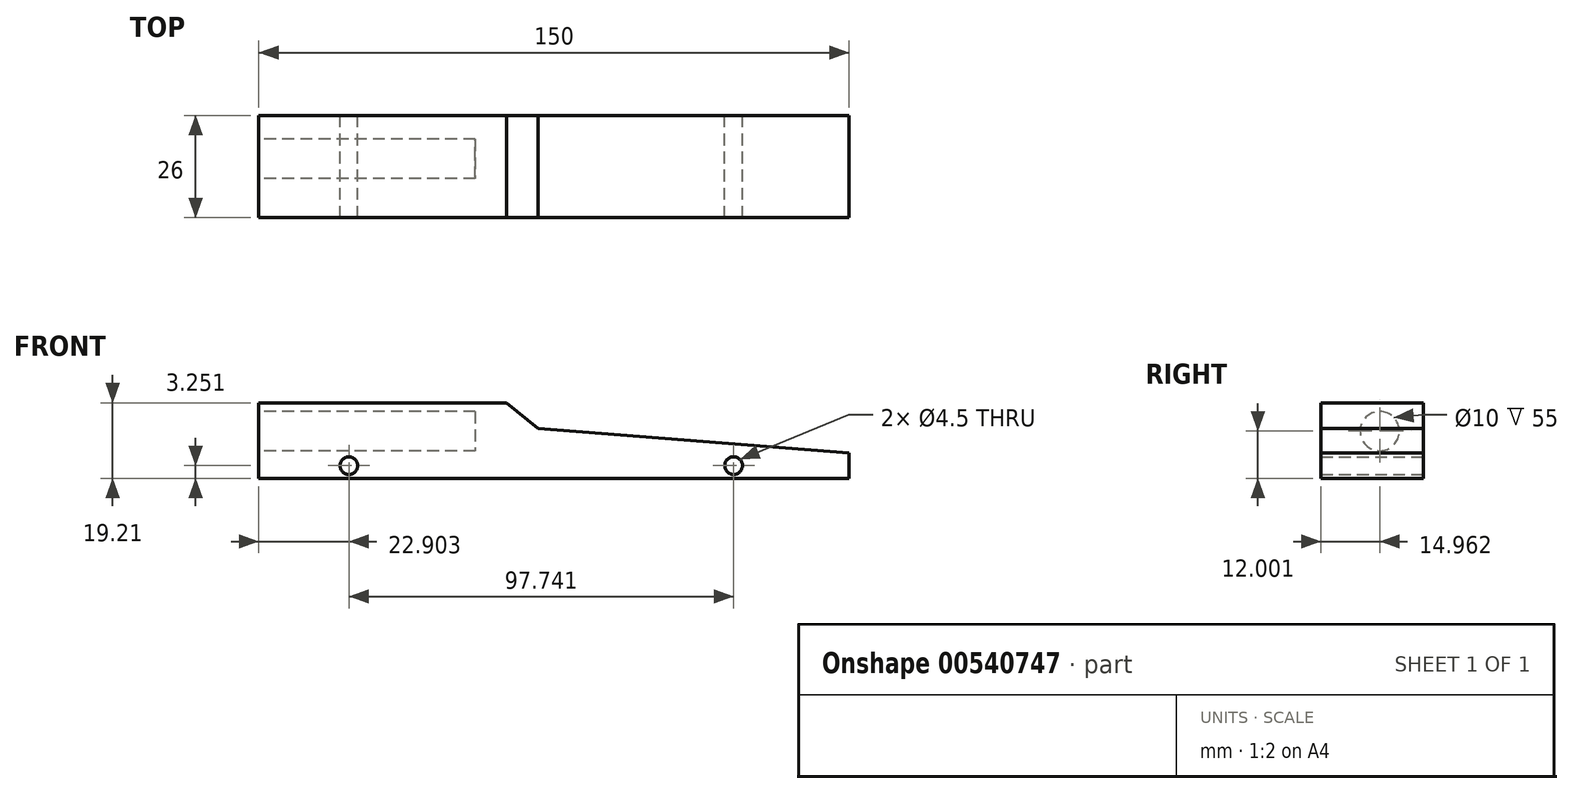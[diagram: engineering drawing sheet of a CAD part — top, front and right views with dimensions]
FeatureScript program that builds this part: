
annotation { "Feature Type Name" : "Feature", "Feature Type Description" : "" }
export const myFeature = defineFeature(function(context is Context, id is Id, definition is map)
    precondition{}
    {
        {
            var Q0;
            Q0=qCreatedBy(makeId("Front.planeOp"),FACE);
            var sketch = newSketch(context, id + "F0", { "sketchPlane" : qUnion([Q0])});
            skLineSegment(sketch, "E0.bottom", {"start": v(-84.2, -32.3) * mm, "end": v(65.8, -32.3) * mm});
            skLineSegment(sketch, "E0.top", {"start": v(-84.2, -12.3) * mm, "end": v(65.8, -12.3) * mm});
            skLineSegment(sketch, "E0.left", {"start": v(-84.2, -32.3) * mm, "end": v(-84.2, -12.3) * mm});
            skLineSegment(sketch, "E0.right", {"start": v(65.8, -32.3) * mm, "end": v(65.8, -12.3) * mm});
            skSolve(sketch);
        }
        {
            var Q0;
            Q0=makeQuery(id+"F0.imprint","IMPRINT",FACE,{"disambiguationData":[TD([[makeQuery(id+"F0.imprint","IMPRINT",EDGE,{"derivedFrom":sQuery(id+"F0.wireOp",EDGE,"E0.bottom")}),1.0]])]});
            extrude(context, id + "F1", {"entities" : qUnion([Q0]), "depth" : 40 * mm, "offsetDistance" : 25 * mm});
        }
        {
            var Q0;
            Q0=makeQuery(id+"F1.opExtrude","SWEPT_FACE",FACE,{"disambiguationData":[OSD([sQuery(id+"F0.wireOp",EDGE,"E0.left")])]});
            var sketch = newSketch(context, id + "F2", { "sketchPlane" : qUnion([Q0])});
            skCircle(sketch, "E1", {"center": v(20, 2.7) * mm, "radius": 5 * mm});
            skSolve(sketch);
        }
        {
            var Q0;
            Q0=makeQuery(id+"F2.imprint","IMPRINT",FACE,{"disambiguationData":[TD([[makeQuery(id+"F2.imprint","IMPRINT",EDGE,{"derivedFrom":sQuery(id+"F2.wireOp",EDGE,"E1")}),1.0]])]});
            extrude(context, id + "F3", {"entities" : qUnion([Q0]), "operationType" : NewBodyOperationType.REMOVE, "oppositeDirection" : true, "depth" : 65 * mm, "offsetDistance" : 25 * mm});
        }
        {
            var Q0;
            Q0=makeQuery(id+"F1.opExtrude","SWEPT_FACE",FACE,{"disambiguationData":[OSD([sQuery(id+"F0.wireOp",EDGE,"E0.top")])]});
            var sketch = newSketch(context, id + "F4", { "sketchPlane" : qUnion([Q0])});
            skLineSegment(sketch, "E2", {"start": v(-84.2, -35) * mm, "end": v(65.8, -35) * mm});
            skLineSegment(sketch, "E3", {"start": v(-84.2, -5) * mm, "end": v(65.8, -5) * mm});
            skSolve(sketch);
        }
        {
            var Q0;
            {var subQ0=sQuery(id+"F4.wireOp",EDGE,"E3");Q0=makeQuery(id+"F4.imprint","IMPRINT",FACE,{"disambiguationData":[TD([[makeQuery(id+"F4.imprint","IMPRINT",EDGE,{"derivedFrom":subQ0}),1.0]])]});}
            var Q1;
            {var subQ0=sQuery(id+"F4.wireOp",EDGE,"E2");Q1=makeQuery(id+"F4.imprint","IMPRINT",FACE,{"disambiguationData":[TD([[makeQuery(id+"F4.imprint","IMPRINT",EDGE,{"derivedFrom":subQ0}),-1.0]])]});}
            extrude(context, id + "F5", {"entities" : qUnion([Q0, Q1]), "operationType" : NewBodyOperationType.REMOVE, "endBound" : BoundingType.THROUGH_ALL, "oppositeDirection" : true, "depth" : 25 * mm, "offsetDistance" : 25 * mm});
        }
        {
            var Q0;
            Q0=makeQuery(id+"F1.opExtrude","SWEPT_FACE",FACE,{"disambiguationData":[OSD([sQuery(id+"F0.wireOp",EDGE,"E0.left")])]});
            var sketch = newSketch(context, id + "F6", { "sketchPlane" : qUnion([Q0])});
            skCircle(sketch, "E4", {"center": v(20.04, -20.3) * mm, "radius": 5 * mm});
            skSolve(sketch);
        }
        {
            var Q0;
            Q0=makeQuery(id+"F6.imprint","IMPRINT",FACE,{"disambiguationData":[TD([[makeQuery(id+"F6.imprint","IMPRINT",EDGE,{"derivedFrom":sQuery(id+"F6.wireOp",EDGE,"E4")}),1.0]])]});
            extrude(context, id + "F7", {"entities" : qUnion([Q0]), "operationType" : NewBodyOperationType.REMOVE, "oppositeDirection" : true, "depth" : 55 * mm, "offsetDistance" : 25 * mm});
        }
        {
            var Q0;
            Q0=makeQuery(id+"F5.boolean.opBoolean","COPY",FACE,{"derivedFrom":makeQuery(id+"F5.opExtrude","SWEPT_FACE",FACE,{"disambiguationData":[OSD([sQuery(id+"F4.wireOp",EDGE,"E3")])]})});
            var sketch = newSketch(context, id + "F8", { "sketchPlane" : qUnion([Q0])});
            skLineSegment(sketch, "E5", {"start": v(84.2, -13.09) * mm, "end": v(21.24, -13.09) * mm});
            skLineSegment(sketch, "E6", {"start": v(21.24, -13.09) * mm, "end": v(13.26, -19.67) * mm});
            skLineSegment(sketch, "E7", {"start": v(-65.8, -25.78) * mm, "end": v(13.26, -19.67) * mm});
            skPoint(sketch, "E8", {"position": v(-65.8, -22.3) * mm});
            skSolve(sketch);
        }
        {
            var Q0;
            {var subQ3=sQuery(id+"F8.wireOp",EDGE,"E5");Q0=makeQuery(id+"F8.imprint","IMPRINT",FACE,{"disambiguationData":[TD([[makeQuery(id+"F8.imprint","IMPRINT",EDGE,{"derivedFrom":subQ3}),-1.0]])]});}
            extrude(context, id + "F9", {"entities" : qUnion([Q0]), "operationType" : NewBodyOperationType.REMOVE, "endBound" : BoundingType.THROUGH_ALL, "oppositeDirection" : true, "depth" : 25 * mm, "offsetDistance" : 25 * mm});
        }
        {
            var Q0;
            Q0=makeQuery(id+"F1.opExtrude","SWEPT_FACE",FACE,{"disambiguationData":[OSD([sQuery(id+"F0.wireOp",EDGE,"E0.left")])]});
            var sketch = newSketch(context, id + "F10", { "sketchPlane" : qUnion([Q0])});
            skLineSegment(sketch, "E9", {"start": v(9, -13.09) * mm, "end": v(9, -32.3) * mm});
            skLineSegment(sketch, "E10", {"start": v(31, -13.09) * mm, "end": v(31, -33.18) * mm});
            skSolve(sketch);
        }
        {
            var Q0;
            {var subQ0=sQuery(id+"F10.wireOp",EDGE,"E9");Q0=makeQuery(id+"F10.imprint","IMPRINT",FACE,{"disambiguationData":[TD([[makeQuery(id+"F10.imprint","IMPRINT",EDGE,{"derivedFrom":subQ0}),-1.0]])]});}
            var Q1;
            {var subQ1=sQuery(id+"F0.wireOp",EDGE,"E0.left");var subQ2=sQuery(id+"F0.wireOp",EDGE,"E0.top");var subQ7=makeQuery(id+"F5.boolean.opBoolean","COPY",EDGE,{"derivedFrom":makeQuery(id+"F5.opExtrude","SWEPT_EDGE",EDGE,{"disambiguationData":[OSD([subQ2,subQ1,sQuery(id+"F4.wireOp",EDGE,"E2")])]})});Q1=makeQuery(id+"F10.imprint","IMPRINT",FACE,{"disambiguationData":[TD([[makeQuery(id+"F10.imprint","IMPRINT",EDGE,{"derivedFrom":subQ7}),1.0]])]});}
            extrude(context, id + "F11", {"entities" : qUnion([Q0, Q1]), "operationType" : NewBodyOperationType.REMOVE, "endBound" : BoundingType.THROUGH_ALL, "oppositeDirection" : true, "depth" : 25 * mm, "offsetDistance" : 25 * mm});
        }
        {
            var Q0;
            Q0=makeQuery(id+"F11.boolean.opBoolean","COPY",FACE,{"derivedFrom":makeQuery(id+"F11.opExtrude","SWEPT_FACE",FACE,{"disambiguationData":[OSD([sQuery(id+"F10.wireOp",EDGE,"E9")])]})});
            var sketch = newSketch(context, id + "F12", { "sketchPlane" : qUnion([Q0])});
            skCircle(sketch, "E11", {"center": v(-36.44, -29.05) * mm, "radius": 2.25 * mm});
            skCircle(sketch, "E12", {"center": v(61.3, -29.05) * mm, "radius": 2.25 * mm});
            skSolve(sketch);
        }
        {
            var Q0;
            Q0=makeQuery(id+"F12.imprint","IMPRINT",FACE,{"disambiguationData":[TD([[makeQuery(id+"F12.imprint","IMPRINT",EDGE,{"derivedFrom":sQuery(id+"F12.wireOp",EDGE,"E11")}),1.0]])]});
            var Q1;
            Q1=makeQuery(id+"F12.imprint","IMPRINT",FACE,{"disambiguationData":[TD([[makeQuery(id+"F12.imprint","IMPRINT",EDGE,{"derivedFrom":sQuery(id+"F12.wireOp",EDGE,"E12")}),1.0]])]});
            extrude(context, id + "F13", {"entities" : qUnion([Q0, Q1]), "operationType" : NewBodyOperationType.REMOVE, "endBound" : BoundingType.THROUGH_ALL, "oppositeDirection" : true, "depth" : 25 * mm, "offsetDistance" : 25 * mm});
        }
    });
